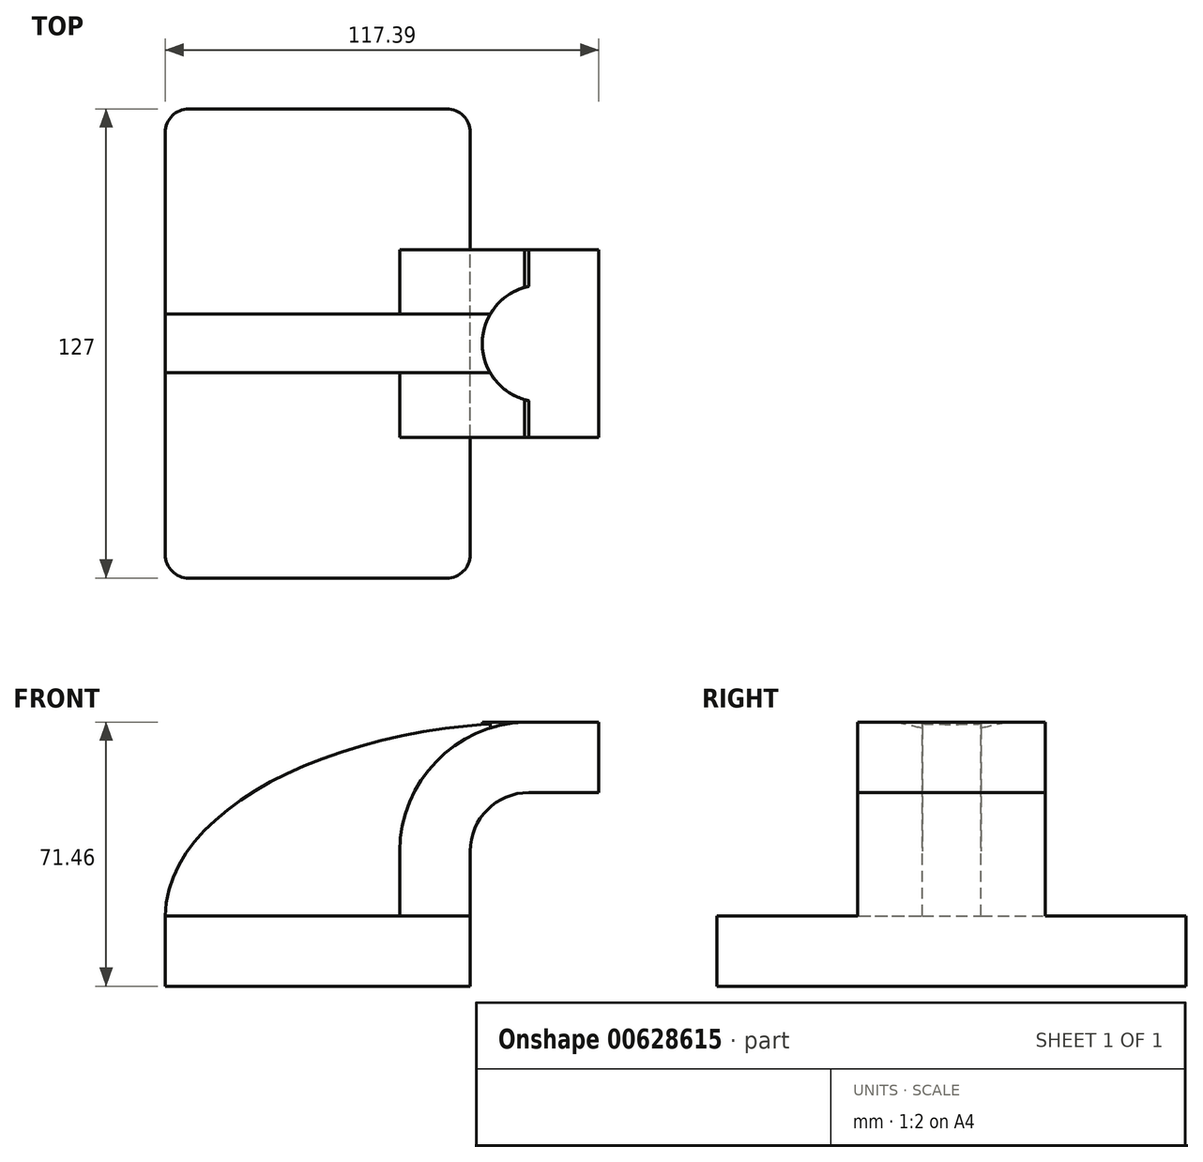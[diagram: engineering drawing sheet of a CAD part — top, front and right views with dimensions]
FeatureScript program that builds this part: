
annotation { "Feature Type Name" : "Feature", "Feature Type Description" : "" }
export const myFeature = defineFeature(function(context is Context, id is Id, definition is map)
    precondition{}
    {
        {
            var Q0;
            Q0=qCreatedBy(makeId("Front.planeOp"),FACE);
            var sketch = newSketch(context, id + "F0", { "sketchPlane" : qUnion([Q0])});
            skLineSegment(sketch, "E0.bottom", {"start": v(-41.28, -9.53) * mm, "end": v(41.28, -9.53) * mm});
            skLineSegment(sketch, "E0.top", {"start": v(-41.28, 9.53) * mm, "end": v(41.28, 9.53) * mm});
            skLineSegment(sketch, "E0.left", {"start": v(-41.28, -9.53) * mm, "end": v(-41.28, 9.53) * mm});
            skLineSegment(sketch, "E0.right", {"start": v(41.28, -9.53) * mm, "end": v(41.28, 9.53) * mm});
            skPoint(sketch, "E0.middle", {"position": v(0, 0) * mm});
            skLineSegment(sketch, "E1.bottom", {"start": v(111.12, 38.1) * mm, "end": v(60.32, 38.1) * mm});
            skLineSegment(sketch, "E1.top", {"start": v(111.12, 66.68) * mm, "end": v(60.32, 66.68) * mm});
            skLineSegment(sketch, "E1.left", {"start": v(111.12, 38.1) * mm, "end": v(111.12, 66.68) * mm});
            skLineSegment(sketch, "E1.right", {"start": v(60.32, 38.1) * mm, "end": v(60.32, 66.68) * mm});
            skPoint(sketch, "E1.middle", {"position": v(85.72, 52.39) * mm});
            skLineSegment(sketch, "E2", {"start": v(41.28, 9.53) * mm, "end": v(41.28, 27) * mm});
            skArc(sketch, "E3", {"start": v(41.27, 27) * mm, "mid": v(45.92, 38.23) * mm, "end": v(57.15, 42.88) * mm});
            skLineSegment(sketch, "E4", {"start": v(57.15, 42.88) * mm, "end": v(76.11, 42.88) * mm});
            skLineSegment(sketch, "E5.0", {"start": v(57.15, 61.93) * mm, "end": v(76.11, 61.93) * mm});
            skArc(sketch, "E5.1", {"start": v(22.23, 27) * mm, "mid": v(32.45, 51.7) * mm, "end": v(57.15, 61.93) * mm});
            skLineSegment(sketch, "E5.2", {"start": v(22.22, 9.53) * mm, "end": v(22.22, 27) * mm});
            skFitSpline(sketch, "E6", {"points": [v(-41.28, 9.52) * mm, v(57.15, 61.93) * mm], "startDerivative": vector(1.81, 88.4) * mm, "endDerivative": vector(156, 2) * mm});
            skLineSegment(sketch, "E7", {"start": v(76.11, 61.93) * mm, "end": v(76.11, 42.88) * mm});
            skLineSegment(sketch, "E8", {"start": v(76.11, 61.93) * mm, "end": v(76.11, 66.68) * mm});
            skLineSegment(sketch, "E9", {"start": v(76.11, 66.68) * mm, "end": v(76.11, 38.1) * mm});
            skSolve(sketch);
        }
        {
            var Q0;
            Q0=makeQuery(id+"F0.imprint","IMPRINT",FACE,{"disambiguationData":[TD([[makeQuery(id+"F0.imprint","IMPRINT",EDGE,{"derivedFrom":sQuery(id+"F0.wireOp",EDGE,"E0.bottom")}),1.0]])]});
            extrude(context, id + "F1", {"entities" : qUnion([Q0]), "endBound" : BoundingType.SYMMETRIC, "depth" : 127 * mm, "offsetDistance" : 25.4 * mm});
        }
        {
            var Q0;
            {var subQ5=sQuery(id+"F0.wireOp",EDGE,"E7");Q0=makeQuery(id+"F0.imprint","IMPRINT",FACE,{"disambiguationData":[TD([[makeQuery(id+"F0.imprint","IMPRINT",EDGE,{"derivedFrom":subQ5}),-1.0]])]});}
            var Q1;
            {var subQ0=sQuery(id+"F0.wireOp",EDGE,"E2");Q1=makeQuery(id+"F0.imprint","IMPRINT",FACE,{"disambiguationData":[TD([[makeQuery(id+"F0.imprint","IMPRINT",EDGE,{"derivedFrom":subQ0}),1.0]])]});}
            extrude(context, id + "F2", {"entities" : qUnion([Q0, Q1]), "operationType" : NewBodyOperationType.ADD, "endBound" : BoundingType.SYMMETRIC, "depth" : 50.8 * mm, "offsetDistance" : 25.4 * mm});
        }
        {
            var Q0;
            {var subQ3=sQuery(id+"F0.wireOp",EDGE,"E5.2");Q0=makeQuery(id+"F0.imprint","IMPRINT",FACE,{"disambiguationData":[TD([[makeQuery(id+"F0.imprint","IMPRINT",EDGE,{"derivedFrom":subQ3}),1.0]])]});}
            extrude(context, id + "F3", {"entities" : qUnion([Q0]), "operationType" : NewBodyOperationType.ADD, "endBound" : BoundingType.SYMMETRIC, "depth" : 15.88 * mm, "offsetDistance" : 25.4 * mm});
        }
        {
            var Q0;
            {var subQ0=sQuery(id+"F0.wireOp",EDGE,"E4");var subQ1=sQuery(id+"F0.wireOp",EDGE,"E1.right");var subQ2=makeQuery(id+"F0.imprint","INTERSECT",VERTEX,{"derivedFrom":[subQ1,subQ0]});Q0=makeQuery(id+"F0.imprint","IMPRINT",FACE,{"disambiguationData":[TD([[makeQuery(id+"F0.imprint","IMPRINT",EDGE,{"disambiguationData":[TD([[subQ2,-1.0]])],"derivedFrom":subQ1}),-1.0]])]});}
            var Q1;
            Q1=sQuery(id+"F0.wireOp",EDGE,"E1.right");
            revolve(context, id + "F4", {"operationType" : NewBodyOperationType.ADD, "entities" : qUnion([Q0]), "axis" : qUnion([Q1]), "revolveType" : RevolveType.FULL});
        }
        {
            var Q0;
            Q0=makeQuery(id+"F1.opExtrude","CAP_EDGE",EDGE,{"disambiguationData":[OSD([sQuery(id+"F0.wireOp",EDGE,"E0.right")])],"isStart":false});
            var Q1;
            Q1=makeQuery(id+"F1.opExtrude","CAP_EDGE",EDGE,{"disambiguationData":[OSD([sQuery(id+"F0.wireOp",EDGE,"E0.left")])],"isStart":false});
            var Q2;
            Q2=makeQuery(id+"F1.opExtrude","CAP_EDGE",EDGE,{"disambiguationData":[OSD([sQuery(id+"F0.wireOp",EDGE,"E0.right")])],"isStart":true});
            var Q3;
            Q3=makeQuery(id+"F1.opExtrude","CAP_EDGE",EDGE,{"disambiguationData":[OSD([sQuery(id+"F0.wireOp",EDGE,"E0.left")])],"isStart":true});
            fillet(context, id + "F5", {"entities" : qUnion([Q0, Q1, Q2, Q3]), "radius" : 6.35 * mm, "tangentPropagation" : true, "allowEdgeOverflow" : false});
        }
    });
